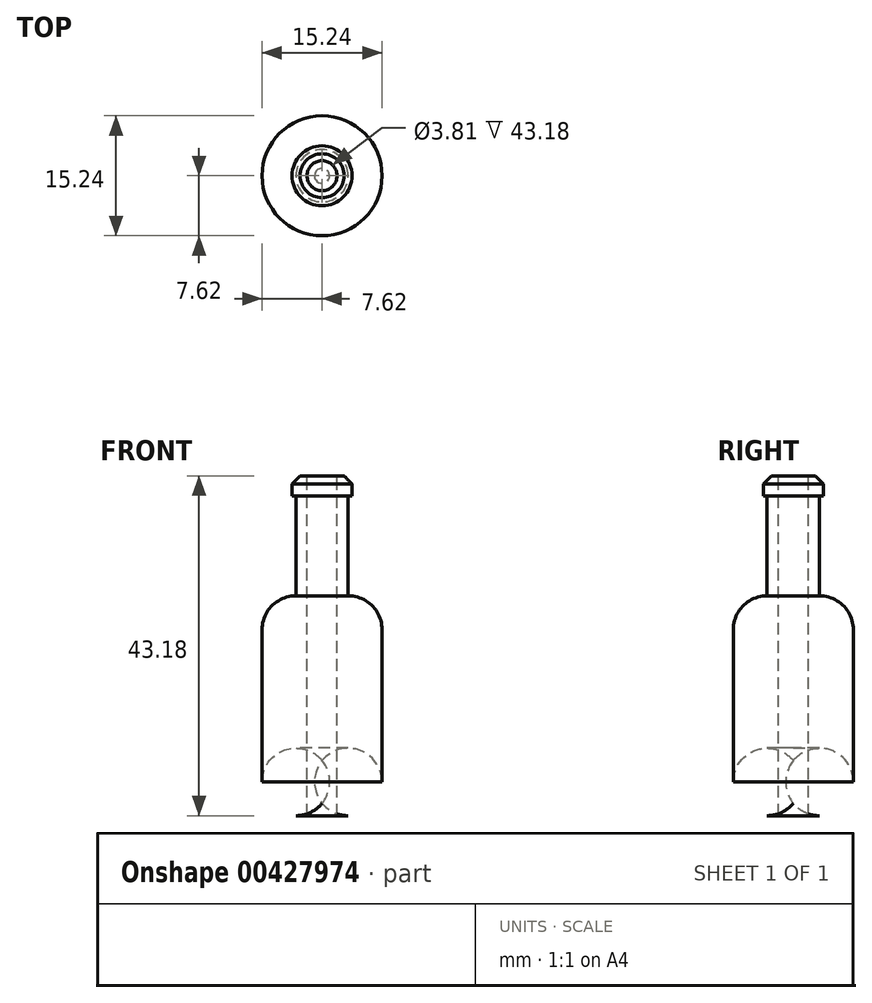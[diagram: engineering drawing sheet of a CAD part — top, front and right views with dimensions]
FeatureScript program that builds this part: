
annotation { "Feature Type Name" : "Feature", "Feature Type Description" : "" }
export const myFeature = defineFeature(function(context is Context, id is Id, definition is map)
    precondition{}
    {
        {
            var Q0;
            Q0=qCreatedBy(makeId("Top.planeOp"),FACE);
            var sketch = newSketch(context, id + "F0", { "sketchPlane" : qUnion([Q0])});
            skCircle(sketch, "E0", {"center": v(0, 0) * mm, "radius": 7.62 * mm});
            skSolve(sketch);
        }
        {
            var Q0;
            Q0 = qSketchRegion(id + "F0", true);
            extrude(context, id + "F1", {"entities" : qUnion([Q0]), "depth" : 27.94 * mm});
        }
        {
            var Q0;
            Q0=makeQuery(id+"F1.opExtrude","CAP_EDGE",EDGE,{"disambiguationData":[OSD([sQuery(id+"F0.wireOp",EDGE,"E0")])],"isStart":true});
            fillet(context, id + "F2", {"entities" : qUnion([Q0]), "radius" : 4.3 * mm, "tangentPropagation" : true, "allowEdgeOverflow" : false});
        }
        {
            var Q0;
            Q0=makeQuery(id+"F1.opExtrude","CAP_FACE",FACE,{"disambiguationData":[OSD([sQuery(id+"F0.wireOp",EDGE,"E0")])],"isStart":false});
            fillet(context, id + "F3", {"entities" : qUnion([Q0]), "radius" : 4.3 * mm, "tangentPropagation" : true, "allowEdgeOverflow" : false});
        }
        {
            var Q0;
            Q0=makeQuery(id+"F1.opExtrude","CAP_FACE",FACE,{"disambiguationData":[OSD([sQuery(id+"F0.wireOp",EDGE,"E0")])],"isStart":false});
            extrude(context, id + "F4", {"entities" : qUnion([Q0]), "operationType" : NewBodyOperationType.ADD, "depth" : 12.7 * mm});
        }
        {
            var Q0;
            Q0=makeQuery(id+"F4.opExtrude","CAP_FACE",FACE,{"disambiguationData":[OSD([sQuery(id+"F0.wireOp",EDGE,"E0")])],"isStart":false});
            var sketch = newSketch(context, id + "F5", { "sketchPlane" : qUnion([Q0])});
            skCircle(sketch, "E1", {"center": v(0, 0) * mm, "radius": 3.81 * mm});
            skSolve(sketch);
        }
        {
            var Q0;
            Q0 = qSketchRegion(id + "F5", true);
            extrude(context, id + "F6", {"entities" : qUnion([Q0]), "operationType" : NewBodyOperationType.ADD, "depth" : 2.54 * mm});
        }
        {
            var Q0;
            Q0=makeQuery(id+"F6.opExtrude","CAP_EDGE",EDGE,{"disambiguationData":[OSD([sQuery(id+"F5.wireOp",EDGE,"E1")])],"isStart":false});
            chamfer(context, id + "F7", {"entities" : qUnion([Q0]), "width" : 1.02 * mm, "tangentPropagation" : true});
        }
        {
            var Q0;
            Q0=makeQuery(id+"F6.opExtrude","CAP_FACE",FACE,{"disambiguationData":[OSD([sQuery(id+"F5.wireOp",EDGE,"E1")])],"isStart":false});
            var sketch = newSketch(context, id + "F8", { "sketchPlane" : qUnion([Q0])});
            skCircle(sketch, "E2", {"center": v(0, 0) * mm, "radius": 1.9 * mm});
            skSolve(sketch);
        }
        {
            var Q0;
            Q0 = qSketchRegion(id + "F8", true);
            extrude(context, id + "F9", {"entities" : qUnion([Q0]), "operationType" : NewBodyOperationType.REMOVE, "oppositeDirection" : true, "depth" : 43.18 * mm});
        }
    });
